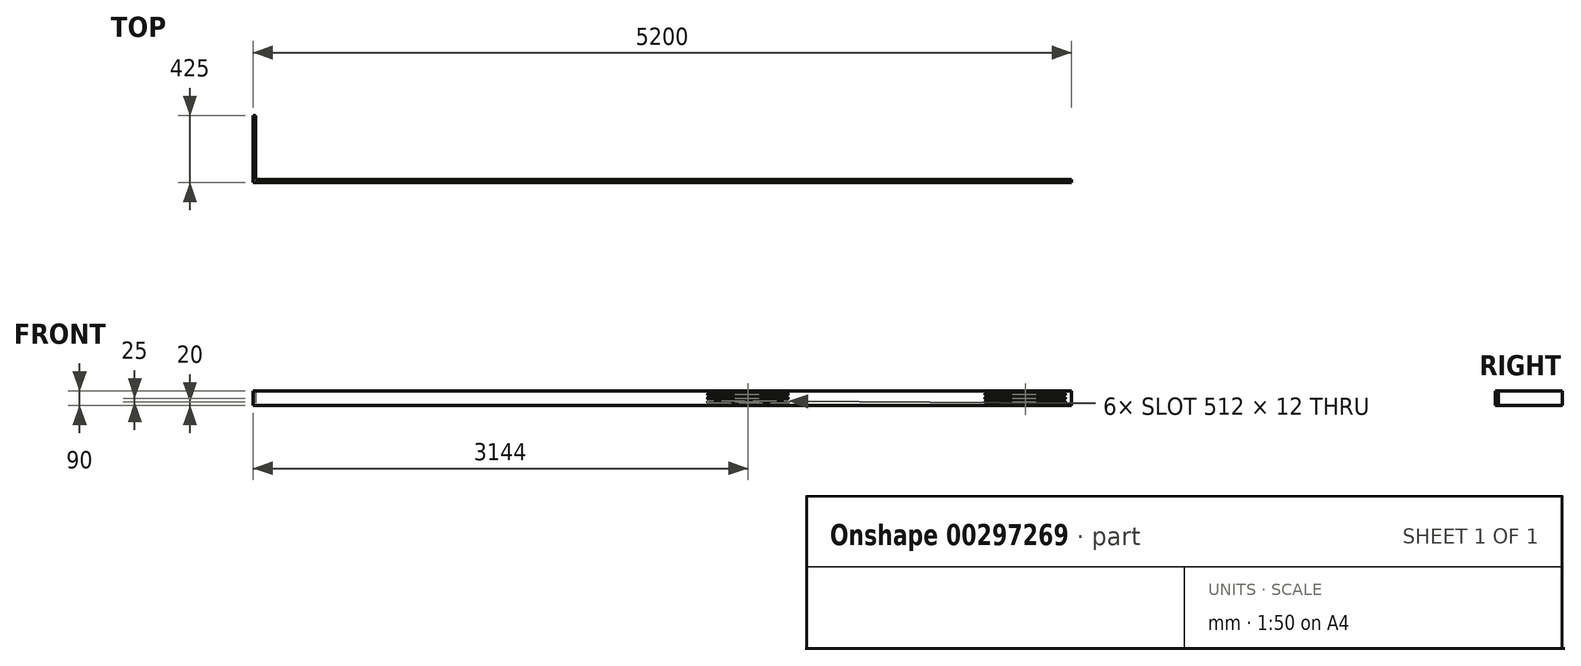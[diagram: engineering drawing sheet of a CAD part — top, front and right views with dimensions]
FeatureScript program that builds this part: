
annotation { "Feature Type Name" : "Feature", "Feature Type Description" : "" }
export const myFeature = defineFeature(function(context is Context, id is Id, definition is map)
    precondition{}
    {
        {
            var Q0;
            Q0=qCreatedBy(makeId("Top.planeOp"),FACE);
            var sketch = newSketch(context, id + "F0", { "sketchPlane" : qUnion([Q0])});
            skLineSegment(sketch, "E0.bottom", {"start": v(2600, 9) * mm, "end": v(-2582, 9) * mm});
            skLineSegment(sketch, "E0.top", {"start": v(2600, -9) * mm, "end": v(-2600, -9) * mm});
            skLineSegment(sketch, "E0.left", {"start": v(2600, 9) * mm, "end": v(2600, -9) * mm});
            skLineSegment(sketch, "E0.right", {"start": v(-2600, 9) * mm, "end": v(-2600, -9) * mm});
            skPoint(sketch, "E0.middle", {"position": v(0, 0) * mm});
            skLineSegment(sketch, "E1.top", {"start": v(-2600, 416) * mm, "end": v(-2582, 416) * mm});
            skLineSegment(sketch, "E1.left", {"start": v(-2600, 9) * mm, "end": v(-2600, 416) * mm});
            skLineSegment(sketch, "E1.right", {"start": v(-2582, 9) * mm, "end": v(-2582, 416) * mm});
            skSolve(sketch);
        }
        {
            var Q0;
            Q0 = qSketchRegion(id + "F0", true);
            extrude(context, id + "F1", {"entities" : qUnion([Q0]), "depth" : 90 * mm});
        }
        {
            var Q0;
            Q0=makeQuery(id+"F1.opExtrude","SWEPT_FACE",FACE,{"disambiguationData":[OSD([sQuery(id+"F0.wireOp",EDGE,"E0.top")])]});
            var sketch = newSketch(context, id + "F2", { "sketchPlane" : qUnion([Q0])});
            skLineSegment(sketch, "E2.bottom", {"start": v(2055, 76) * mm, "end": v(2555, 76) * mm});
            skLineSegment(sketch, "E2.top", {"start": v(2055, 64) * mm, "end": v(2555, 64) * mm});
            skArc(sketch, "E3", {"start": v(2055, 76) * mm, "mid": v(2049, 70) * mm, "end": v(2055, 64) * mm});
            skArc(sketch, "E4", {"start": v(2555, 64) * mm, "mid": v(2561, 70) * mm, "end": v(2555, 76) * mm});
            skLineSegment(sketch, "E5.0.1.0", {"start": v(2055, 51) * mm, "end": v(2555, 51) * mm});
            skLineSegment(sketch, "E5.0.1.1", {"start": v(2055, 39) * mm, "end": v(2555, 39) * mm});
            skArc(sketch, "E5.0.1.2", {"start": v(2555, 39) * mm, "mid": v(2561, 45) * mm, "end": v(2555, 51) * mm});
            skArc(sketch, "E5.0.1.3", {"start": v(2055, 51) * mm, "mid": v(2049, 45) * mm, "end": v(2055, 39) * mm});
            skLineSegment(sketch, "E5.0.2.0", {"start": v(2055, 26) * mm, "end": v(2555, 26) * mm});
            skLineSegment(sketch, "E5.0.2.1", {"start": v(2055, 14) * mm, "end": v(2555, 14) * mm});
            skArc(sketch, "E5.0.2.2", {"start": v(2555, 14) * mm, "mid": v(2561, 20) * mm, "end": v(2555, 26) * mm});
            skArc(sketch, "E5.0.2.3", {"start": v(2055, 26) * mm, "mid": v(2049, 20) * mm, "end": v(2055, 14) * mm});
            skLineSegment(sketch, "E5.direction1", {"start": v(2025, 64) * mm, "end": v(2055, 64) * mm, "construction": true});
            skLineSegment(sketch, "E5.direction2", {"start": v(2055, 64) * mm, "end": v(2055, 39) * mm, "construction": true});
            skLineSegment(sketch, "E6.bottom", {"start": v(294, 76) * mm, "end": v(794, 76) * mm});
            skLineSegment(sketch, "E6.top", {"start": v(294, 64) * mm, "end": v(794, 64) * mm});
            skArc(sketch, "E7", {"start": v(294, 76) * mm, "mid": v(288, 70) * mm, "end": v(294, 64) * mm});
            skArc(sketch, "E8", {"start": v(794, 64) * mm, "mid": v(800, 70) * mm, "end": v(794, 76) * mm});
            skLineSegment(sketch, "E9.0.1.0", {"start": v(294, 51) * mm, "end": v(794, 51) * mm});
            skLineSegment(sketch, "E9.0.1.1", {"start": v(294, 39) * mm, "end": v(794, 39) * mm});
            skArc(sketch, "E9.0.1.2", {"start": v(794, 39) * mm, "mid": v(800, 45) * mm, "end": v(794, 51) * mm});
            skArc(sketch, "E9.0.1.3", {"start": v(294, 51) * mm, "mid": v(288, 45) * mm, "end": v(294, 39) * mm});
            skLineSegment(sketch, "E9.0.2.0", {"start": v(294, 26) * mm, "end": v(794, 26) * mm});
            skLineSegment(sketch, "E9.0.2.1", {"start": v(294, 14) * mm, "end": v(794, 14) * mm});
            skArc(sketch, "E9.0.2.2", {"start": v(794, 14) * mm, "mid": v(800, 20) * mm, "end": v(794, 26) * mm});
            skArc(sketch, "E9.0.2.3", {"start": v(294, 26) * mm, "mid": v(288, 20) * mm, "end": v(294, 14) * mm});
            skLineSegment(sketch, "E9.direction1", {"start": v(226.5, 64) * mm, "end": v(294, 64) * mm, "construction": true});
            skLineSegment(sketch, "E9.direction2", {"start": v(294, 64) * mm, "end": v(294, 39) * mm, "construction": true});
            skSolve(sketch);
        }
        {
            var Q0;
            Q0 = qSketchRegion(id + "F2", true);
            extrude(context, id + "F3", {"entities" : qUnion([Q0]), "operationType" : NewBodyOperationType.REMOVE, "oppositeDirection" : true, "depth" : 18 * mm});
        }
    });
